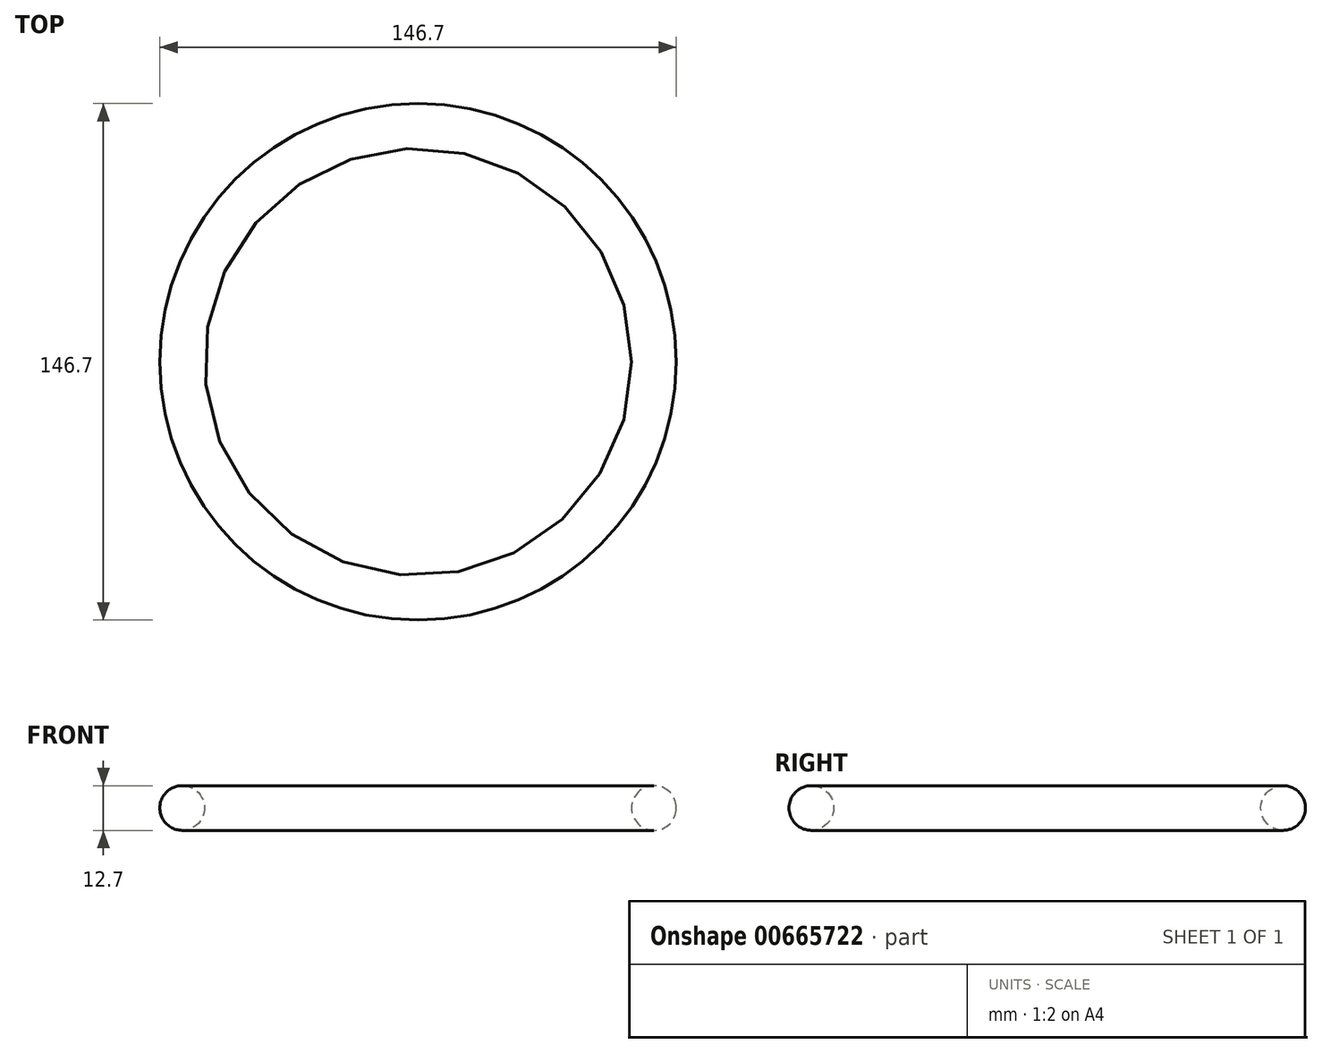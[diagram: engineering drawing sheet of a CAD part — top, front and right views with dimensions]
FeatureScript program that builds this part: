
annotation { "Feature Type Name" : "Feature", "Feature Type Description" : "" }
export const myFeature = defineFeature(function(context is Context, id is Id, definition is map)
    precondition{}
    {
        {
            var Q0;
            Q0=qCreatedBy(makeId("Right.planeOp"),FACE);
            var sketch = newSketch(context, id + "F0", { "sketchPlane" : qUnion([Q0])});
            skCircle(sketch, "E0", {"center": v(-67, 0) * mm, "radius": 6.35 * mm});
            skLineSegment(sketch, "E1", {"start": v(0, 3.15) * mm, "end": v(0, -2.34) * mm});
            skLineSegment(sketch, "E2", {"start": v(-60.65, 0) * mm, "end": v(0, 0) * mm});
            skSolve(sketch);
        }
        {
            var Q0;
            Q0=makeQuery(id+"F0.imprint","IMPRINT",FACE,{"disambiguationData":[TD([[makeQuery(id+"F0.imprint","IMPRINT",EDGE,{"derivedFrom":sQuery(id+"F0.wireOp",EDGE,"E0")}),1.0]])]});
            var Q1;
            Q1=sQuery(id+"F0.wireOp",EDGE,"E1");
            revolve(context, id + "F1", {"entities" : qUnion([Q0]), "axis" : qUnion([Q1]), "revolveType" : RevolveType.FULL});
        }
    });
